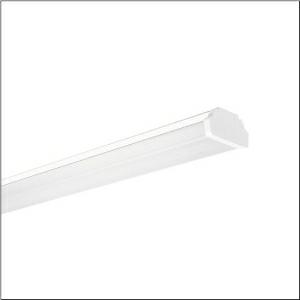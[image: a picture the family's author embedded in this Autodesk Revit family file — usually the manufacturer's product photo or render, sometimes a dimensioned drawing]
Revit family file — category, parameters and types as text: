
# Revit family: dus_r__31_ho_53bd812m1v4120_db1b
name_source: partatom
category: Lighting Fixtures
units: mm (PartAtom-declared; Revit-internal decimal feet)

## family parameters
Cut with Voids When Loaded = No
Host = Face
Light Source = No
Part Type = Normal
Room Calculation Point = No
Round Connector Dimension = Use Diameter
Shared = No

## types (1)
- --- (1 x LED, 12380 lm, 77.3 W, 4000K)
    Apparent Load = 77 VA
    CIE Flux Codes = 47 80 95 92 100
    Color Rendering = 80
    Color Temperature = 4000K
    Default Elevation = 1800 mm
    Description = DUS® 31 HOluminaire insert, length: 1.535mm, width: 81mm, height: 90mm, LED rated luminous flux: 12.380lm, light colour: 840, control gear: ON/OFF Multilumen, control gear: ECG Multilumen, with plug, 3-pole, with phase selection, mains connection: 220..240V, AC, 50/60Hz, primary optical cover: cover, of PMMA, light emission: direct distribution, primary light characteristic: symmetric, protection rating (complete): IP20, protection rating (LED compartment): IP50, insulation class (complete): insulation class I (protective earthing), certification: CE, ENEC, VDE, permissible ambient temperature for indoor applications: -35..+35°C, corresponds to IFS (International Featured Standards) requirements for safety and quality in the food industry, reducing of maximum allowable ambient temperature of 5°C with ceiling mounting, packaging unit: 1 piece
    Height = 95 mm
    Lamp = 1 x LED
    Lamp Light Flux = 12380 lm
    Lamp Power = 77.3 W
    Lamp count = 1
    Length = 1535 mm
    Luminous efficacy = 160 lm/W
    Manufacturer = Siteco
    ModVariant = No
    Model = 53BD812M1V4120
    Mounting Place = Ceiling
    Mounting Type = Pendant
    Number of Poles = 1
    OnlyDefault = Yes
    Power Factor = 1
    Product Name = DUS® 31 HO
    Product group = luminaire insert
    ProductGroupID = 902
    Protection Class = Protection class I
    Protection Degree = IP 20
    RLX_Detail_Level = 1
    RlxData = <blob elided: 39637 chars, md5=76115743>
    Socket = socket
    Standby Power = 0 W
    System Light Flux = 12380 lm
    System Power = 77 W
    Type Comments = factory setting: luminous flux: 100 % | (A | C | E) | 173 mA
    Type Image = l_1003451.jpg
    URL = http://relux.com
    VarID = @adj_133587
    Voltage = 0 V
    Weight = 0.00 kg
    Width = 81 mm

## geometry (parser evidence)
native form markers: Blend x4, Sweep x10
no freeform markers — native parametric forms only
